# Revit family: STH20535_27_30_40
name_source: partatom
category: Luminárias
units: mm (PartAtom-declared; Revit-internal decimal feet)

## family parameters
Com base no plano de trabalho = Não
Compartilhado = Não
Corte com vazios quando carregada = Não
Cota do conector redondo = Utilizar diâmetro
Fonte luminosa = Sim
Manter orientação da anotação = Não
Ponto de cálculo do ambiente = Não
Sempre na vertical = Sim
Tipo de parte = Normal

## types (3) — shared parameters
Altura = 0.05 m
Cromado = Cromado
Diâmetro = 0.05 m
Fabricante = Stella
Filtro de cor = 16777215
Grau de proteção (IP) = IP20
Modelo = Dicroica MR16 EVO
AR70 PRO 7º 4,7W
AR 70 PRO 7º 4,7W
Potência = 6 W
Troca de temperatura da cor de lâmpada com esmaecimento = <Nenhum>
URL = https://stella.com.br
Vidro = Vidro
Ângulo de Abertura = 36°
Ângulo de inclinação = 90.00°
zero-valued in all types: Elevação padrão

## per-type parameters (varying)
| type | Arquivo de rede fotométrica | Dimerização | Fluxo Luminoso | IRC (Índice de reprodução de cores) | Referência | Temperatura da cor (K) | Tensão Elétrica |
| STH20535/27 - BIVOLT - 2700K - 450lm - 36° | STELLA - STH20535-27 - DICROICA MR16 EVO 6W.ies | Não dimerizável | 450 lm | >95 (R9 >80) | STH20535/27 - BIVOLT | 2700 K | 100V-240V |
| STH20535/30 - BIVOLT - 3000K - 450lm - 36° | STELLA - STH20535-30 - DICROICA MR16 EVO 6W.ies | Não dimerizável | 450 lm | >95 (R9 >80) | STH20535/30 - BIVOLT | 3000 K | 100V-240V |
| STH20535/40 - BIVOLT - 4000K - 500lm - 36° | STELLA - STH20535-40 - DICROICA MR16 EVO 6W.ies |  | 500 lm |  | STH20535/40 - BIVOLT | 4000 K | BIVOLT |
